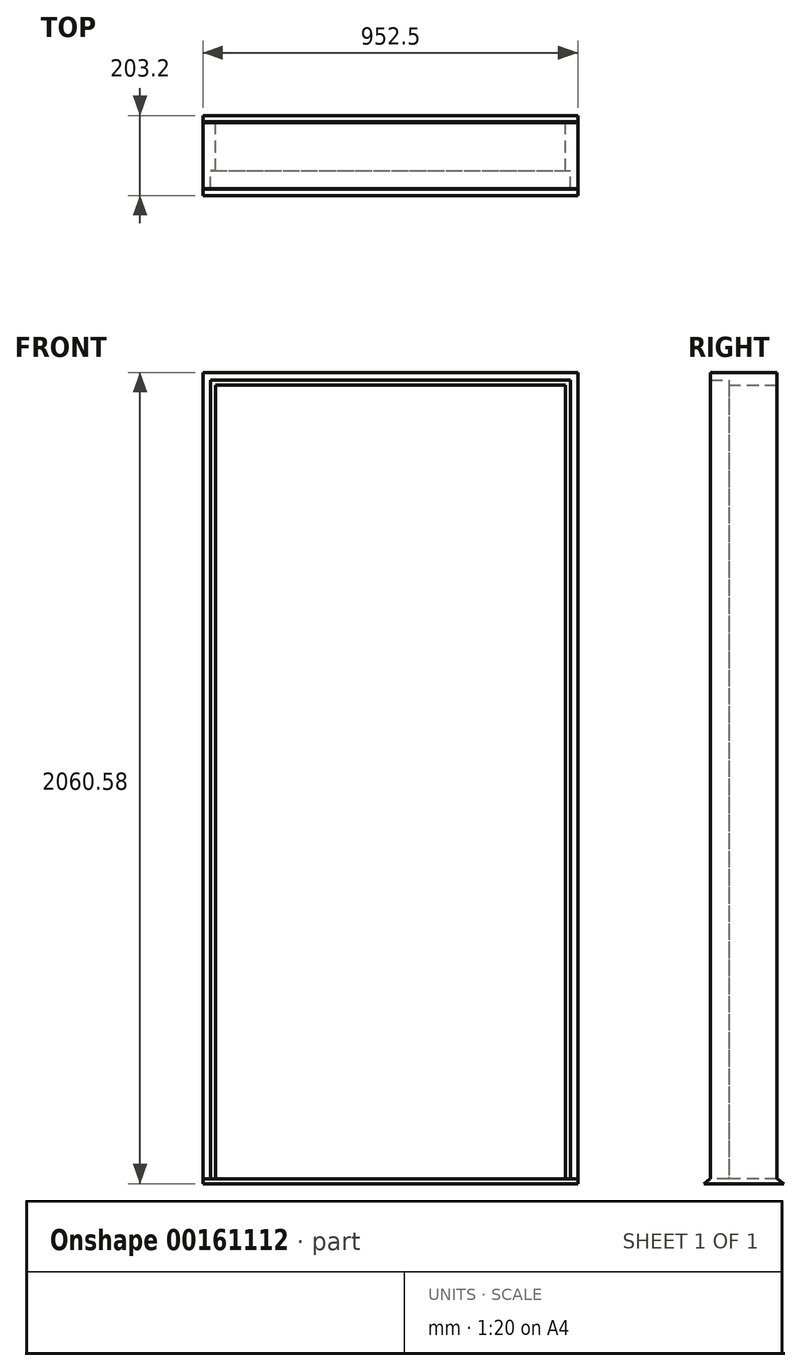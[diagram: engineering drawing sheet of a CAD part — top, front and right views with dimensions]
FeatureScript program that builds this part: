
annotation { "Feature Type Name" : "Feature", "Feature Type Description" : "" }
export const myFeature = defineFeature(function(context is Context, id is Id, definition is map)
    precondition{}
    {
        {
            var Q0;
            Q0=qCreatedBy(makeId("Top.planeOp"),FACE);
            var sketch = newSketch(context, id + "F0", { "sketchPlane" : qUnion([Q0])});
            skLineSegment(sketch, "E0", {"start": v(0, 0) * mm, "end": v(0, 168.28) * mm});
            skLineSegment(sketch, "E1", {"start": v(-31.75, 46.04) * mm, "end": v(-19.05, 46.04) * mm});
            skLineSegment(sketch, "E2", {"start": v(-19.05, 46.04) * mm, "end": v(-19.05, 0) * mm});
            skLineSegment(sketch, "E3", {"start": v(-19.05, 0) * mm, "end": v(0, 0) * mm});
            skLineSegment(sketch, "E4", {"start": v(-476.25, 0) * mm, "end": v(-476.25, 102.45) * mm, "construction": true});
            skLineSegment(sketch, "E5", {"start": v(0, 168.28) * mm, "end": v(-31.75, 168.28) * mm});
            skLineSegment(sketch, "E6", {"start": v(-31.75, 168.28) * mm, "end": v(-31.75, 46.04) * mm});
            skLineSegment(sketch, "E7.MirrorCS", {"start": v(-933.45, 46.04) * mm, "end": v(-933.45, 0) * mm});
            skLineSegment(sketch, "E8.MirrorCS", {"start": v(-920.75, 46.04) * mm, "end": v(-933.45, 46.04) * mm});
            skLineSegment(sketch, "E9.MirrorCS", {"start": v(-920.75, 168.28) * mm, "end": v(-920.75, 46.04) * mm});
            skLineSegment(sketch, "E10.MirrorCS", {"start": v(-952.5, 168.28) * mm, "end": v(-920.75, 168.28) * mm});
            skLineSegment(sketch, "E11.MirrorCS", {"start": v(-952.5, 0) * mm, "end": v(-952.5, 168.28) * mm});
            skLineSegment(sketch, "E12.MirrorCS", {"start": v(-933.45, 0) * mm, "end": v(-952.5, 0) * mm});
            skSolve(sketch);
        }
        {
            var Q0;
            Q0=qSketchRegion(id+"F0",true);
            extrude(context, id + "F1", {"entities" : qUnion([Q0]), "depth" : 2047.87 * mm});
        }
        {
            var Q0;
            Q0=qCreatedBy(makeId("Front.planeOp"),FACE);
            var sketch = newSketch(context, id + "F2", { "sketchPlane" : qUnion([Q0])});
            skPoint(sketch, "E13.0", {"position": v(-952.5, 2047.88) * mm});
            skPoint(sketch, "E14.0", {"position": v(0, 2047.88) * mm});
            skLineSegment(sketch, "E15", {"start": v(-952.5, 2047.88) * mm, "end": v(-476.25, 1571.63) * mm});
            skLineSegment(sketch, "E16", {"start": v(-476.25, 1571.63) * mm, "end": v(0, 2047.88) * mm});
            skLineSegment(sketch, "E17", {"start": v(-952.5, 2047.88) * mm, "end": v(0, 2047.88) * mm});
            skSolve(sketch);
        }
        {
            var Q0;
            Q0=qSketchRegion(id+"F2",true);
            extrude(context, id + "F3", {"entities" : qUnion([Q0]), "operationType" : NewBodyOperationType.REMOVE, "endBound" : BoundingType.THROUGH_ALL, "oppositeDirection" : true, "depth" : 25.4 * mm});
        }
        {
            var Q0;
            Q0=qCreatedBy(makeId("Right.planeOp"),FACE);
            var sketch = newSketch(context, id + "F4", { "sketchPlane" : qUnion([Q0])});
            skLineSegment(sketch, "E18.0", {"start": v(168.28, 2016.13) * mm, "end": v(168.28, 2047.88) * mm});
            skLineSegment(sketch, "E19.0", {"start": v(46.04, 2016.13) * mm, "end": v(168.28, 2016.13) * mm});
            skLineSegment(sketch, "E20.0", {"start": v(46.04, 2028.83) * mm, "end": v(46.04, 2016.13) * mm});
            skLineSegment(sketch, "E21.0", {"start": v(0, 2028.83) * mm, "end": v(46.04, 2028.83) * mm});
            skLineSegment(sketch, "E22.0", {"start": v(0, 2028.83) * mm, "end": v(0, 2047.88) * mm});
            skLineSegment(sketch, "E23.0", {"start": v(0, 2047.88) * mm, "end": v(168.28, 2047.88) * mm});
            skSolve(sketch);
        }
        {
            var Q0;
            Q0=qSketchRegion(id+"F4",true);
            var Q1;
            Q1=makeQuery(id+"F1.opExtrude","SWEPT_FACE",FACE,{"disambiguationData":[OSD([sQuery(id+"F0.wireOp",EDGE,"E11.MirrorCS")])]});
            extrude(context, id + "F5", {"entities" : qUnion([Q0]), "operationType" : NewBodyOperationType.ADD, "endBound" : BoundingType.UP_TO_SURFACE, "oppositeDirection" : true, "endBoundEntityFace" : qUnion([Q1]), "depth" : 914.4 * mm});
        }
        {
            var Q0;
            Q0=qCreatedBy(makeId("Right.planeOp"),FACE);
            var sketch = newSketch(context, id + "F6", { "sketchPlane" : qUnion([Q0])});
            skPoint(sketch, "E24.0", {"position": v(84.14, 0) * mm});
            skLineSegment(sketch, "E25", {"start": v(84.14, 0) * mm, "end": v(84.14, -12.7) * mm, "construction": true});
            skLineSegment(sketch, "E26", {"start": v(84.14, -12.7) * mm, "end": v(185.74, -12.7) * mm});
            skLineSegment(sketch, "E27", {"start": v(185.74, -12.7) * mm, "end": v(169.86, 0) * mm});
            skLineSegment(sketch, "E28", {"start": v(169.86, 0) * mm, "end": v(84.14, 0) * mm});
            skLineSegment(sketch, "E29.MirrorCS", {"start": v(-1.59, 0) * mm, "end": v(84.14, 0) * mm});
            skLineSegment(sketch, "E30.MirrorCS", {"start": v(84.14, -12.7) * mm, "end": v(-17.46, -12.7) * mm});
            skLineSegment(sketch, "E31.MirrorCS", {"start": v(-17.46, -12.7) * mm, "end": v(-1.59, 0) * mm});
            skSolve(sketch);
        }
        {
            var Q0;
            Q0 = qSketchRegion(id + "F6", true);
            var Q1;
            Q1=makeQuery(id+"F1.opExtrude","SWEPT_FACE",FACE,{"disambiguationData":[OSD([sQuery(id+"F0.wireOp",EDGE,"E11.MirrorCS")])]});
            extrude(context, id + "F7", {"entities" : qUnion([Q0]), "operationType" : NewBodyOperationType.ADD, "endBound" : BoundingType.UP_TO_SURFACE, "oppositeDirection" : true, "endBoundEntityFace" : qUnion([Q1]), "depth" : 25.4 * mm});
        }
    });
